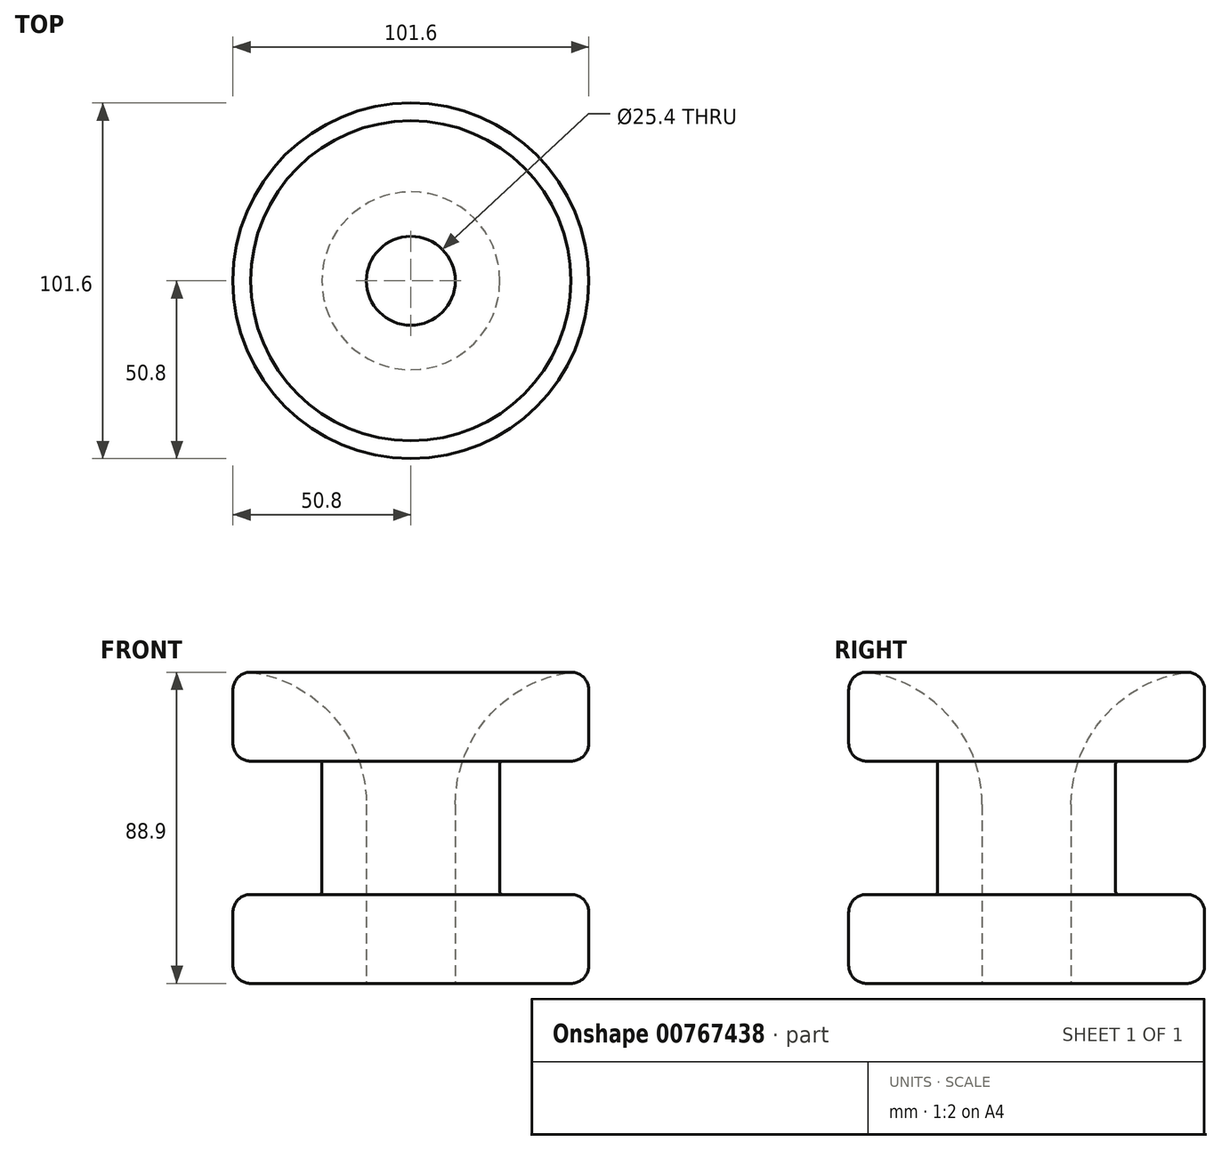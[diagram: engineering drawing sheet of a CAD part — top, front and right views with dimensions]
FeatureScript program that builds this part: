
annotation { "Feature Type Name" : "Feature", "Feature Type Description" : "" }
export const myFeature = defineFeature(function(context is Context, id is Id, definition is map)
    precondition{}
    {
        {
            assignVariable(context, id + "F0", {"name" : "Filet", "anyValue" : .75});
        }
        {
            var Q0;
            Q0=qCreatedBy(makeId("Front.planeOp"),FACE);
            var sketch = newSketch(context, id + "F1", { "sketchPlane" : qUnion([Q0])});
            skLineSegment(sketch, "E0", {"start": v(0, -44.45) * mm, "end": v(0, 44.45) * mm});
            skLineSegment(sketch, "E1", {"start": v(0, 44.45) * mm, "end": v(50.8, 44.45) * mm});
            skLineSegment(sketch, "E2", {"start": v(50.8, 44.45) * mm, "end": v(50.8, 19.05) * mm});
            skLineSegment(sketch, "E3", {"start": v(50.8, -44.45) * mm, "end": v(0, -44.45) * mm});
            skLineSegment(sketch, "E4", {"start": v(50.8, 19.05) * mm, "end": v(25.4, 19.05) * mm});
            skLineSegment(sketch, "E5", {"start": v(25.4, 19.05) * mm, "end": v(25.4, 0) * mm});
            skLineSegment(sketch, "E6", {"start": v(25.4, 0) * mm, "end": v(100.42, 0) * mm, "construction": true});
            skLineSegment(sketch, "E7.MirrorCS", {"start": v(25.4, -19.05) * mm, "end": v(25.4, 0) * mm});
            skLineSegment(sketch, "E8.MirrorCS", {"start": v(50.8, -19.05) * mm, "end": v(25.4, -19.05) * mm});
            skLineSegment(sketch, "E9.trimOffspring", {"start": v(50.8, -19.05) * mm, "end": v(50.8, -44.45) * mm});
            skSolve(sketch);
        }
        {
            var Q0;
            Q0=makeQuery(id+"F1.imprint","IMPRINT",FACE,{"disambiguationData":[TD([[makeQuery(id+"F1.imprint","IMPRINT",EDGE,{"derivedFrom":sQuery(id+"F1.wireOp",EDGE,"E0")}),-1.0]])]});
            var Q1;
            Q1=sQuery(id+"F1.wireOp",EDGE,"E0");
            revolve(context, id + "F2", {"surfaceOperationType" : NewSurfaceOperationType.NEW, "entities" : qUnion([Q0]), "axis" : qUnion([Q1]), "revolveType" : RevolveType.FULL});
        }
        {
            var Q0;
            Q0=makeQuery(id+"F2.opRevolve","SWEPT_EDGE",EDGE,{"disambiguationData":[OSD([sQuery(id+"F1.wireOp",EDGE,"E4"),sQuery(id+"F1.wireOp",EDGE,"E5")])]});
            var Q1;
            Q1=makeQuery(id+"F2.opRevolve","SWEPT_EDGE",EDGE,{"disambiguationData":[OSD([sQuery(id+"F1.wireOp",EDGE,"E7.MirrorCS"),sQuery(id+"F1.wireOp",EDGE,"E8.MirrorCS")])]});
            fillet(context, id + "F3", {"entities" : qUnion([Q0, Q1]), "radius" : (getVariable(context, 'Filet')) * mm, "tangentPropagation" : true, "allowEdgeOverflow" : false});
        }
        {
            var Q0;
            Q0=makeQuery(id+"F2.opRevolve","SWEPT_EDGE",EDGE,{"disambiguationData":[OSD([sQuery(id+"F1.wireOp",EDGE,"E2"),sQuery(id+"F1.wireOp",EDGE,"E4")])]});
            var Q1;
            Q1=makeQuery(id+"F2.opRevolve","SWEPT_EDGE",EDGE,{"disambiguationData":[OSD([sQuery(id+"F1.wireOp",EDGE,"E1"),sQuery(id+"F1.wireOp",EDGE,"E2")])]});
            var Q2;
            Q2=makeQuery(id+"F2.opRevolve","SWEPT_EDGE",EDGE,{"disambiguationData":[OSD([sQuery(id+"F1.wireOp",EDGE,"E3"),sQuery(id+"F1.wireOp",EDGE,"E9.trimOffspring")])]});
            var Q3;
            Q3=makeQuery(id+"F2.opRevolve","SWEPT_EDGE",EDGE,{"disambiguationData":[OSD([sQuery(id+"F1.wireOp",EDGE,"E8.MirrorCS"),sQuery(id+"F1.wireOp",EDGE,"E9.trimOffspring")])]});
            fillet(context, id + "F4", {"entities" : qUnion([Q0, Q1, Q2, Q3]), "radius" : 5.08 * mm, "tangentPropagation" : true, "allowEdgeOverflow" : false});
        }
        {
            var Q0;
            Q0=makeQuery(id+"F2.opRevolve","SWEPT_FACE",FACE,{"disambiguationData":[OSD([sQuery(id+"F1.wireOp",EDGE,"E3")])]});
            var sketch = newSketch(context, id + "F5", { "sketchPlane" : qUnion([Q0])});
            skCircle(sketch, "E10", {"center": v(0, 0) * mm, "radius": 12.7 * mm});
            skSolve(sketch);
        }
        {
            var Q0;
            Q0=makeQuery(id+"F5.imprint","IMPRINT",FACE,{"disambiguationData":[TD([[makeQuery(id+"F5.imprint","IMPRINT",EDGE,{"derivedFrom":sQuery(id+"F5.wireOp",EDGE,"E10")}),1.0]])]});
            extrude(context, id + "F6", {"entities" : qUnion([Q0]), "operationType" : NewBodyOperationType.REMOVE, "endBound" : BoundingType.THROUGH_ALL, "oppositeDirection" : true, "depth" : 25.4 * mm, "offsetDistance" : 25.4 * mm});
        }
        {
            var Q0;
            Q0=makeQuery(id+"F6.boolean.opBoolean","INTERSECT",EDGE,{"derivedFrom":[makeQuery(id+"F2.opRevolve","SWEPT_FACE",FACE,{"disambiguationData":[OSD([sQuery(id+"F1.wireOp",EDGE,"E1")])]}),makeQuery(id+"F6.opExtrude","SWEPT_FACE",FACE,{"disambiguationData":[OSD([sQuery(id+"F5.wireOp",EDGE,"E10")])]})]});
            var Q1;
            Q1=makeQuery(id+"F6.boolean.opBoolean","COPY",EDGE,{"derivedFrom":makeQuery(id+"F6.opExtrude","CAP_EDGE",EDGE,{"disambiguationData":[OSD([sQuery(id+"F5.wireOp",EDGE,"E10")])],"isStart":true})});
            fillet(context, id + "F7", {"entities" : qUnion([Q0, Q1]), "radius" : 38.1 * mm, "tangentPropagation" : true, "allowEdgeOverflow" : false});
        }
    });
